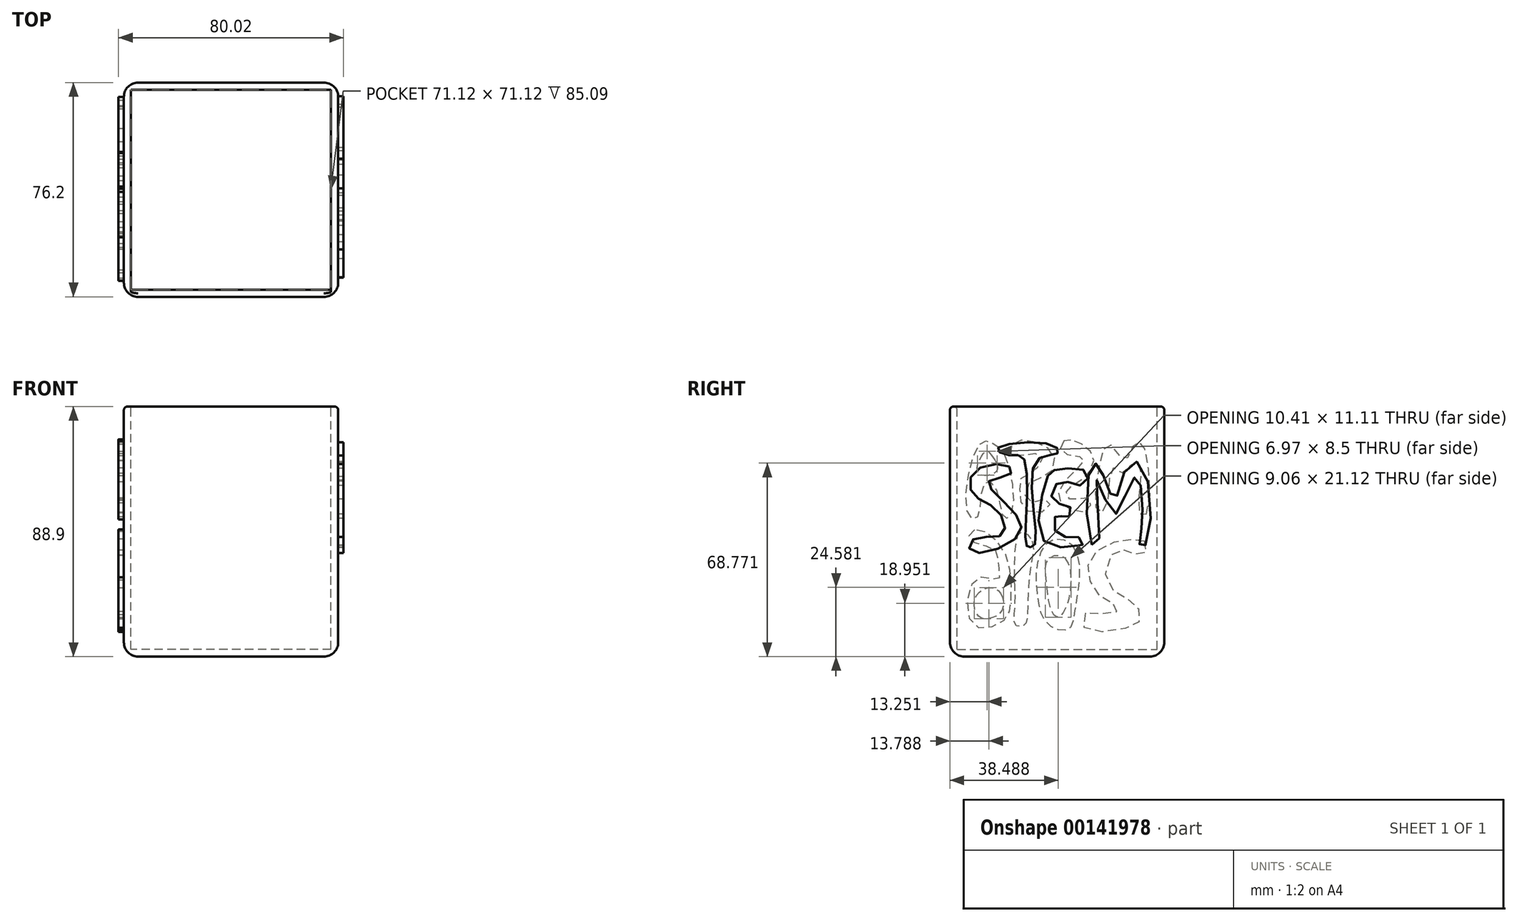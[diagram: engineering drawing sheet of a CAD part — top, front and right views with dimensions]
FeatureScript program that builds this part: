
annotation { "Feature Type Name" : "Feature", "Feature Type Description" : "" }
export const myFeature = defineFeature(function(context is Context, id is Id, definition is map)
    precondition{}
    {
        {
            var Q0;
            Q0=qCreatedBy(makeId("Top.planeOp"),FACE);
            var sketch = newSketch(context, id + "F0", { "sketchPlane" : qUnion([Q0])});
            skLineSegment(sketch, "E0.bottom", {"start": v(38.1, -38.1) * mm, "end": v(-38.1, -38.1) * mm});
            skLineSegment(sketch, "E0.top", {"start": v(38.1, 38.1) * mm, "end": v(-38.1, 38.1) * mm});
            skLineSegment(sketch, "E0.left", {"start": v(38.1, -38.1) * mm, "end": v(38.1, 38.1) * mm});
            skLineSegment(sketch, "E0.right", {"start": v(-38.1, -38.1) * mm, "end": v(-38.1, 38.1) * mm});
            skPoint(sketch, "E0.middle", {"position": v(0, 0) * mm});
            skSolve(sketch);
        }
        {
            var Q0;
            Q0=makeQuery(id+"F0.imprint","IMPRINT",FACE,{"disambiguationData":[TD([[makeQuery(id+"F0.imprint","IMPRINT",EDGE,{"derivedFrom":sQuery(id+"F0.wireOp",EDGE,"E0.bottom")}),-1.0]])]});
            extrude(context, id + "F1", {"entities" : qUnion([Q0]), "oppositeDirection" : true, "depth" : 88.9 * mm});
        }
        {
            var Q0;
            Q0=makeQuery(id+"F1.opExtrude","CAP_FACE",FACE,{"disambiguationData":[OSD([sQuery(id+"F0.wireOp",EDGE,"E0.bottom"),sQuery(id+"F0.wireOp",EDGE,"E0.top"),sQuery(id+"F0.wireOp",EDGE,"E0.left"),sQuery(id+"F0.wireOp",EDGE,"E0.right")])],"isStart":true});
            shell(context, id + "F2", {"entities" : qUnion([Q0]), "thickness" : 2.54 * mm});
        }
        {
            var Q0;
            Q0=makeQuery(id+"F1.opExtrude","SWEPT_EDGE",EDGE,{"disambiguationData":[OSD([sQuery(id+"F0.wireOp",EDGE,"E0.top"),sQuery(id+"F0.wireOp",EDGE,"E0.left")])]});
            var Q1;
            Q1=makeQuery(id+"F1.opExtrude","SWEPT_EDGE",EDGE,{"disambiguationData":[OSD([sQuery(id+"F0.wireOp",EDGE,"E0.top"),sQuery(id+"F0.wireOp",EDGE,"E0.right")])]});
            var Q2;
            Q2=makeQuery(id+"F1.opExtrude","SWEPT_EDGE",EDGE,{"disambiguationData":[OSD([sQuery(id+"F0.wireOp",EDGE,"E0.bottom"),sQuery(id+"F0.wireOp",EDGE,"E0.left")])]});
            var Q3;
            Q3=makeQuery(id+"F1.opExtrude","SWEPT_EDGE",EDGE,{"disambiguationData":[OSD([sQuery(id+"F0.wireOp",EDGE,"E0.bottom"),sQuery(id+"F0.wireOp",EDGE,"E0.right")])]});
            fillet(context, id + "F3", {"entities" : qUnion([Q0, Q1, Q2, Q3]), "radius" : 5.08 * mm, "tangentPropagation" : true, "allowEdgeOverflow" : false});
        }
        {
            var Q0;
            Q0=makeQuery(id+"F1.opExtrude","CAP_EDGE",EDGE,{"disambiguationData":[OSD([sQuery(id+"F0.wireOp",EDGE,"E0.top")])],"isStart":true});
            fillet(context, id + "F4", {"entities" : qUnion([Q0]), "radius" : 1.27 * mm, "tangentPropagation" : true, "allowEdgeOverflow" : false});
        }
        {
            var Q0;
            {var subQ0=sQuery(id+"F0.wireOp",EDGE,"E0.bottom");Q0=makeQuery(id+"F2.opShell","OFFSET_EDGE",EDGE,{"disambiguationData":[OSD([subQ0]),TDD([makeQuery(id+"F1.opExtrude","CAP_EDGE",EDGE,{"disambiguationData":[OSD([subQ0])],"isStart":true})])]});}
            fillet(context, id + "F5", {"entities" : qUnion([Q0]), "radius" : 1.27 * mm, "tangentPropagation" : true, "allowEdgeOverflow" : false});
        }
        {
            var Q0;
            Q0=makeQuery(id+"F1.opExtrude","CAP_FACE",FACE,{"disambiguationData":[OSD([sQuery(id+"F0.wireOp",EDGE,"E0.bottom"),sQuery(id+"F0.wireOp",EDGE,"E0.top"),sQuery(id+"F0.wireOp",EDGE,"E0.left"),sQuery(id+"F0.wireOp",EDGE,"E0.right")])],"isStart":false});
            fillet(context, id + "F6", {"entities" : qUnion([Q0]), "radius" : 5.08 * mm, "tangentPropagation" : true, "allowEdgeOverflow" : false});
        }
        {
            var Q0;
            Q0=makeQuery(id+"F1.opExtrude","SWEPT_FACE",FACE,{"disambiguationData":[OSD([sQuery(id+"F0.wireOp",EDGE,"E0.left")])]});
            var sketch = newSketch(context, id + "F7", { "sketchPlane" : qUnion([Q0])});
            skFitSpline(sketch, "E1", {"points": [v(-17, -21.4) * mm, v(-16.7, -24.05) * mm, v(-24.45, -26.8) * mm, v(-16.3, -36.5) * mm, v(-13.95, -46.08) * mm, v(-30.47, -51.48) * mm, v(-29.55, -47) * mm, v(-19.45, -45.57) * mm, v(-20.98, -37.2) * mm, v(-29.96, -31.09) * mm, v(-29.14, -22.93) * mm, v(-17, -21.4) * mm]});
            skFitSpline(sketch, "E2", {"points": [v(-11.7, -18.75) * mm, v(-11.1, -48.93) * mm, v(-10.07, -49.95) * mm, v(-7.93, -49.14) * mm, v(-7.73, -19.77) * mm, v(0, -16.71) * mm, v(-1.1, -13.96) * mm, v(-21.19, -14.88) * mm, v(-17, -17.32) * mm, v(-11.7, -18.75) * mm]});
            skFitSpline(sketch, "E3", {"points": [v(-3.24, -24.67) * mm, v(-4.06, -48.42) * mm, v(8.9, -49.34) * mm, v(9, -49.44) * mm, v(8.38, -46.9) * mm, v(0, -45.36) * mm, v(0, -38.33) * mm, v(3.18, -39.76) * mm, v(4.92, -36.09) * mm, v(-1.5, -33.43) * mm, v(0.94, -26.7) * mm, v(8.8, -27.93) * mm, v(10.63, -23.34) * mm, v(0, -22.42) * mm, v(-3.24, -24.67) * mm]});
            skFitSpline(sketch, "E4", {"points": [v(12.26, -49.14) * mm, v(12.36, -20.48) * mm, v(14.3, -20.8) * mm, v(17.46, -27.21) * mm, v(20.62, -32.92) * mm, v(25.1, -21) * mm, v(30.2, -21.2) * mm, v(31.84, -48.53) * mm, v(29.6, -50.05) * mm, v(29.7, -45.26) * mm, v(30.3, -35.07) * mm, v(28.27, -24.87) * mm, v(23.47, -33.43) * mm, v(19.9, -38.02) * mm, v(14, -26.2) * mm, v(14.5, -49.14) * mm, v(12.26, -49.14) * mm]});
            skSolve(sketch);
        }
        {
            var Q0;
            Q0 = qSketchRegion(id + "F7", true);
            extrude(context, id + "F8", {"entities" : qUnion([Q0]), "depth" : 1.9 * mm});
        }
        {
            var Q0;
            Q0=makeQuery(id+"F1.opExtrude","SWEPT_FACE",FACE,{"disambiguationData":[OSD([sQuery(id+"F0.wireOp",EDGE,"E0.right")])]});
            var sketch = newSketch(context, id + "F9", { "sketchPlane" : qUnion([Q0])});
            skFitSpline(sketch, "E5", {"points": [v(18.73, -17.27) * mm, v(16.13, -37.42) * mm, v(18.73, -39.61) * mm, v(22.16, -28.24) * mm, v(26, -27.55) * mm, v(28.46, -39.61) * mm, v(31.75, -37.97) * mm, v(27.37, -13.16) * mm, v(23.25, -12.88) * mm, v(18.73, -17.27) * mm]});
            skFitSpline(sketch, "E6", {"points": [v(23.4, -17.27) * mm, v(21.47, -22.89) * mm, v(28.05, -23.57) * mm, v(25.45, -16.03) * mm, v(23.4, -17.27) * mm]});
            skFitSpline(sketch, "E7", {"points": [v(-31.72, -38.24) * mm, v(-31.3, -15.35) * mm, v(-29.25, -12.74) * mm, v(-26.65, -14.66) * mm, v(-24.04, -19.05) * mm, v(-18.56, -13.43) * mm, v(-14.58, -23.03) * mm, v(-14.45, -37.15) * mm, v(-17.33, -36.46) * mm, v(-19.66, -21.8) * mm, v(-23.36, -23.57) * mm, v(-27.33, -19.46) * mm, v(-29.66, -20.83) * mm, v(-29.25, -38.24) * mm, v(-31.72, -38.24) * mm]});
            skFitSpline(sketch, "E8", {"points": [v(-2.38, -12.2) * mm, v(-1.83, -16.3) * mm, v(-9.51, -18.36) * mm, v(-2.8, -26.45) * mm, v(-1.29, -34.13) * mm, v(-11.02, -36.87) * mm, v(-11.16, -32.62) * mm, v(-5.12, -33.17) * mm, v(-3.34, -30.02) * mm, v(-9.37, -25.5) * mm, v(-12.94, -18.23) * mm, v(-7.87, -12.88) * mm, v(-2.38, -12.2) * mm]});
            skFitSpline(sketch, "E9", {"points": [v(7.76, -12.74) * mm, v(15.44, -12.88) * mm, v(16.54, -16.86) * mm, v(9.96, -16.86) * mm, v(5.16, -17.82) * mm, v(9.27, -23.71) * mm, v(12.7, -25.22) * mm, v(13.25, -30.57) * mm, v(11.33, -36.6) * mm, v(3.38, -36.46) * mm, v(3.24, -33.03) * mm, v(9.82, -34) * mm, v(10.5, -27.82) * mm, v(2.55, -23.71) * mm, v(1.32, -17.13) * mm, v(7.76, -12.74) * mm]});
            skSolve(sketch);
        }
        {
            var Q0;
            Q0 = qSketchRegion(id + "F9", true);
            extrude(context, id + "F10", {"entities" : qUnion([Q0]), "depth" : 1.9 * mm});
        }
        {
            var Q0;
            Q0=makeQuery(id+"F1.opExtrude","SWEPT_FACE",FACE,{"disambiguationData":[OSD([sQuery(id+"F0.wireOp",EDGE,"E0.right")])]});
            var sketch = newSketch(context, id + "F11", { "sketchPlane" : qUnion([Q0])});
            skFitSpline(sketch, "E10", {"points": [v(-30.98, -47.72) * mm, v(-31.53, -51.76) * mm, v(-28.78, -52.68) * mm, v(-24.38, -51.21) * mm, v(-19.97, -51.94) * mm, v(-17.4, -61.86) * mm, v(-24.01, -67.91) * mm, v(-28.78, -71.58) * mm, v(-29.15, -76.54) * mm, v(-22, -79.3) * mm, v(-9.7, -78.74) * mm, v(-10.61, -73.05) * mm, v(-18.5, -73.97) * mm, v(-21.8, -71.58) * mm, v(-17.59, -69.2) * mm, v(-12.26, -63.14) * mm, v(-11.16, -55.8) * mm, v(-17.4, -49.2) * mm, v(-26.95, -47.17) * mm, v(-30.98, -47.72) * mm]});
            skFitSpline(sketch, "E11", {"points": [v(-5.3, -49.2) * mm, v(-7.86, -60.57) * mm, v(-6.2, -73.05) * mm, v(-4.37, -78.92) * mm, v(0, -79.3) * mm, v(4.8, -75.44) * mm, v(7, -66.44) * mm, v(7, -56.17) * mm, v(2.23, -47.54) * mm, v(-5.3, -49.2) * mm]});
            skFitSpline(sketch, "E12", {"points": [v(-2.72, -53.78) * mm, v(-3.82, -69.56) * mm, v(0, -74.89) * mm, v(2.42, -71.4) * mm, v(3.7, -63.14) * mm, v(3.15, -54.33) * mm, v(-2.72, -53.78) * mm]});
            skFitSpline(sketch, "E13", {"points": [v(8.84, -47.9) * mm, v(9.4, -56.9) * mm, v(10.5, -72.32) * mm, v(11.78, -78) * mm, v(14.9, -77.64) * mm, v(15.08, -72.5) * mm, v(15.08, -62.4) * mm, v(14.9, -51.03) * mm, v(12.7, -44.42) * mm, v(8.84, -47.9) * mm]});
            skFitSpline(sketch, "E14", {"points": [v(29.4, -43.87) * mm, v(31.05, -47.17) * mm, v(22.42, -50.66) * mm, v(21.14, -54.88) * mm, v(20.95, -61.49) * mm, v(28.48, -61.1) * mm, v(30.13, -77.27) * mm, v(18.92, -75.98) * mm, v(16.35, -67.9) * mm, v(19.1, -50.99) * mm, v(29.4, -43.87) * mm]});
            skFitSpline(sketch, "E15", {"points": [v(20.02, -66.43) * mm, v(19.65, -72.5) * mm, v(24.43, -75.43) * mm, v(28.1, -74.33) * mm, v(29.21, -68.27) * mm, v(24.25, -64.4) * mm, v(20.02, -66.43) * mm]});
            skSolve(sketch);
        }
        {
            var Q0;
            Q0 = qSketchRegion(id + "F11", true);
            extrude(context, id + "F12", {"entities" : qUnion([Q0]), "depth" : 1.9 * mm});
        }
    });
